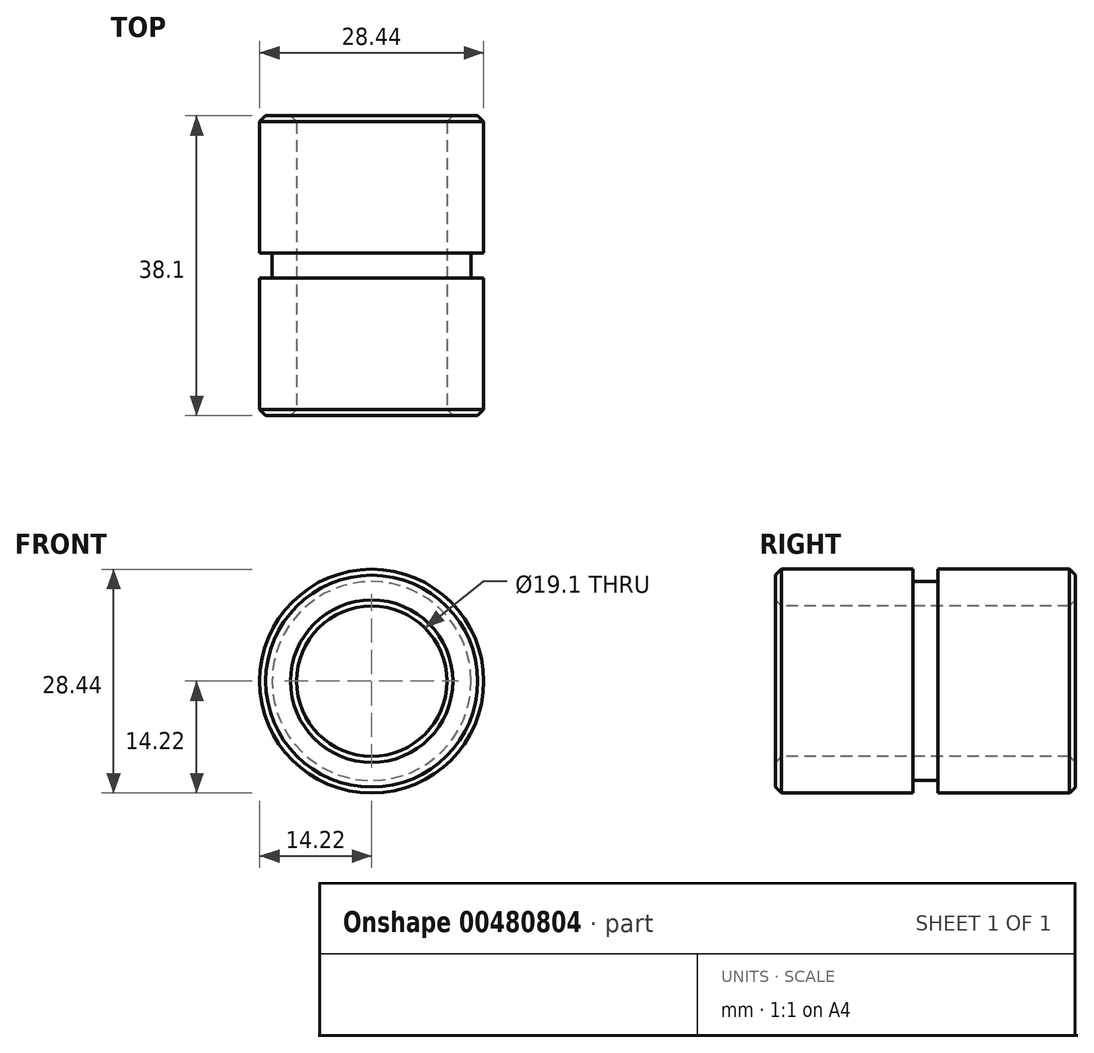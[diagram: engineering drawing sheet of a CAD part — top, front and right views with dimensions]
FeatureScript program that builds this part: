
annotation { "Feature Type Name" : "Feature", "Feature Type Description" : "" }
export const myFeature = defineFeature(function(context is Context, id is Id, definition is map)
    precondition{}
    {
        {
            var Q0;
            Q0=qCreatedBy(makeId("Front.planeOp"),FACE);
            var sketch = newSketch(context, id + "F0", { "sketchPlane" : qUnion([Q0])});
            skCircle(sketch, "E0", {"center": v(0, 0) * mm, "radius": 14.22 * mm});
            skCircle(sketch, "E1", {"center": v(0, 0) * mm, "radius": 9.55 * mm});
            skSolve(sketch);
        }
        {
            var Q0;
            Q0 = qSketchRegion(id + "F0", true);
            extrude(context, id + "F1", {"entities" : qUnion([Q0]), "endBound" : BoundingType.SYMMETRIC, "oppositeDirection" : true, "depth" : 38.1 * mm});
        }
        {
            var Q0;
            Q0=qCreatedBy(makeId("Front.planeOp"),FACE);
            var sketch = newSketch(context, id + "F2", { "sketchPlane" : qUnion([Q0])});
            skCircle(sketch, "E2", {"center": v(0, 0) * mm, "radius": 14.22 * mm});
            skCircle(sketch, "E3", {"center": v(0, 0) * mm, "radius": 12.64 * mm});
            skSolve(sketch);
        }
        {
            var Q0;
            Q0=makeQuery(id+"F2.imprint","IMPRINT",FACE,{"disambiguationData":[TD([[makeQuery(id+"F2.imprint","IMPRINT",EDGE,{"derivedFrom":sQuery(id+"F2.wireOp",EDGE,"E2")}),1.0]])]});
            extrude(context, id + "F3", {"entities" : qUnion([Q0]), "operationType" : NewBodyOperationType.REMOVE, "endBound" : BoundingType.SYMMETRIC, "depth" : 3.17 * mm});
        }
        {
            var Q0;
            Q0=makeQuery(id+"F1.opExtrude","CAP_EDGE",EDGE,{"disambiguationData":[OSD([sQuery(id+"F0.wireOp",EDGE,"E0")])],"isStart":true});
            var Q1;
            Q1=makeQuery(id+"F1.opExtrude","CAP_EDGE",EDGE,{"disambiguationData":[OSD([sQuery(id+"F0.wireOp",EDGE,"E0")])],"isStart":false});
            var Q2;
            Q2=makeQuery(id+"F1.opExtrude","CAP_EDGE",EDGE,{"disambiguationData":[OSD([sQuery(id+"F0.wireOp",EDGE,"E1")])],"isStart":true});
            var Q3;
            Q3=makeQuery(id+"F1.opExtrude","CAP_EDGE",EDGE,{"disambiguationData":[OSD([sQuery(id+"F0.wireOp",EDGE,"E1")])],"isStart":false});
            chamfer(context, id + "F4", {"entities" : qUnion([Q0, Q1, Q2, Q3]), "width" : 0.76 * mm, "tangentPropagation" : true});
        }
    });
